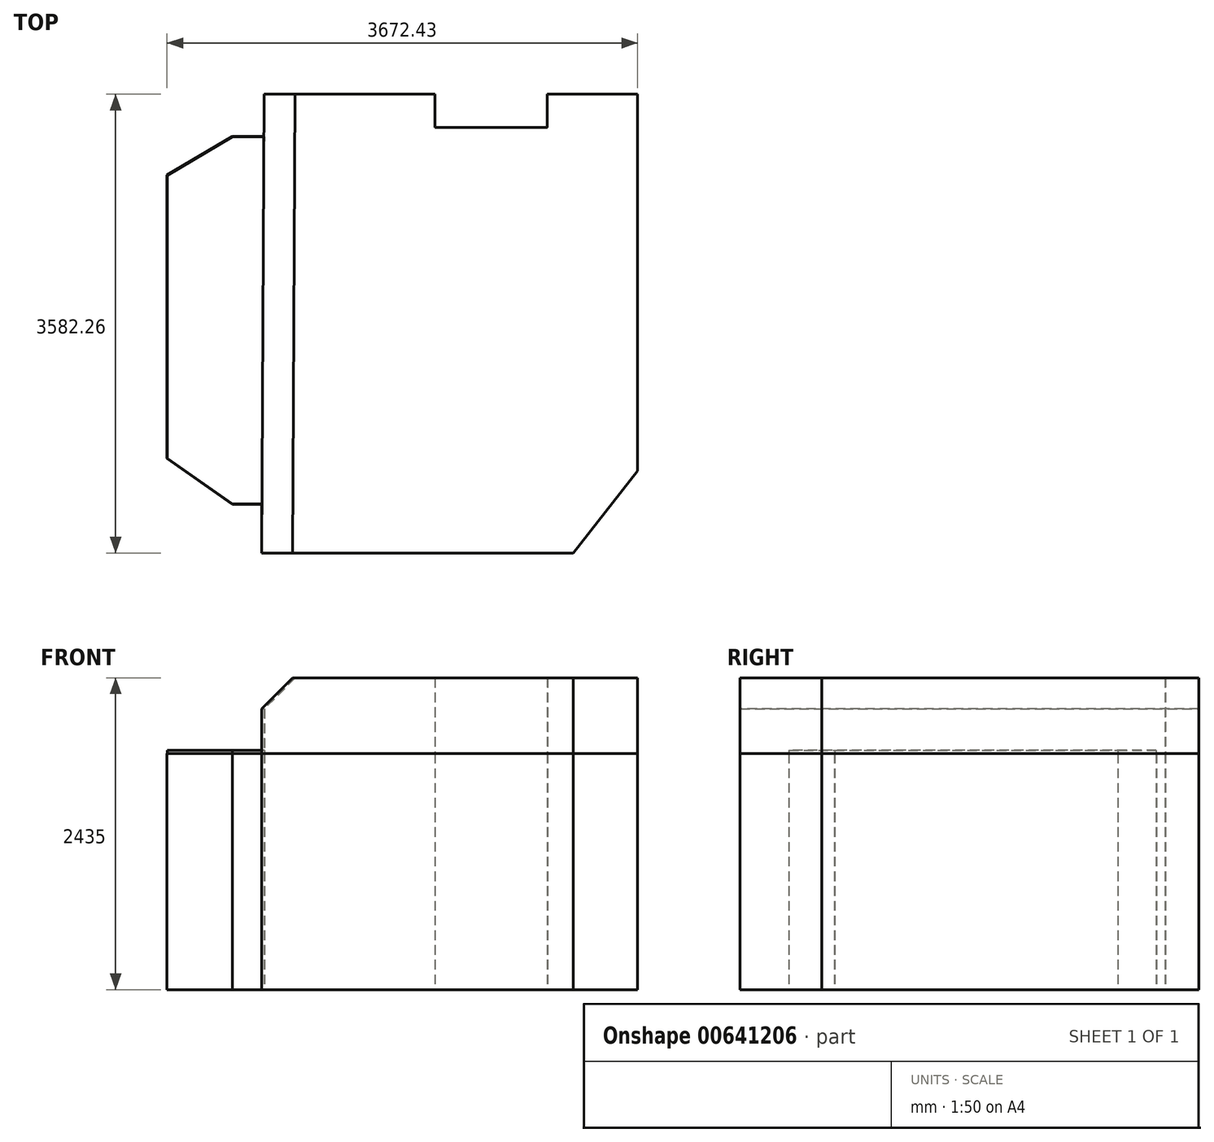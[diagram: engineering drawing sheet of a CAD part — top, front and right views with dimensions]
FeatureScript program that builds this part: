
annotation { "Feature Type Name" : "Feature", "Feature Type Description" : "" }
export const myFeature = defineFeature(function(context is Context, id is Id, definition is map)
    precondition{}
    {
        {
            var Q0;
            Q0=qCreatedBy(makeId("Top.planeOp"),FACE);
            var sketch = newSketch(context, id + "F0", { "sketchPlane" : qUnion([Q0])});
            skLineSegment(sketch, "E0", {"start": v(0, 0) * mm, "end": v(2430, 0) * mm});
            skLineSegment(sketch, "E1", {"start": v(0, 0) * mm, "end": v(0, 380) * mm});
            skLineSegment(sketch, "E2", {"start": v(0, 380) * mm, "end": v(-230, 380) * mm});
            skLineSegment(sketch, "E3", {"start": v(-230, 380) * mm, "end": v(-737.43, 736.24) * mm});
            skLineSegment(sketch, "E4", {"start": v(-737.43, 736.24) * mm, "end": v(-737.43, 2946.24) * mm});
            skLineSegment(sketch, "E5", {"start": v(-737.43, 2946.24) * mm, "end": v(-230, 3247.26) * mm});
            skLineSegment(sketch, "E6", {"start": v(-230, 3247.26) * mm, "end": v(20, 3247.26) * mm});
            skLineSegment(sketch, "E7", {"start": v(20, 3247.26) * mm, "end": v(20, 3577.26) * mm});
            skLineSegment(sketch, "E8", {"start": v(20, 3577.26) * mm, "end": v(1350, 3577.26) * mm});
            skLineSegment(sketch, "E9", {"start": v(1350, 3577.26) * mm, "end": v(1350, 3317.26) * mm});
            skLineSegment(sketch, "E10", {"start": v(1350, 3317.26) * mm, "end": v(2230, 3317.26) * mm});
            skLineSegment(sketch, "E11", {"start": v(2230, 3317.26) * mm, "end": v(2230, 3577.26) * mm});
            skLineSegment(sketch, "E12", {"start": v(2230, 3577.26) * mm, "end": v(2930, 3577.26) * mm});
            skLineSegment(sketch, "E13", {"start": v(2930, 3577.26) * mm, "end": v(2930, 637.26) * mm});
            skLineSegment(sketch, "E14", {"start": v(2930, 637.26) * mm, "end": v(2430, 0) * mm});
            skSolve(sketch);
        }
        {
            var Q0;
            Q0 = qSketchRegion(id + "F0", true);
            extrude(context, id + "F1", {"entities" : qUnion([Q0]), "depth" : 1840 * mm, "offsetDistance" : 25 * mm});
        }
        {
            var Q0;
            Q0=makeQuery(id+"F1.opExtrude","CAP_FACE",FACE,{"disambiguationData":[OSD([sQuery(id+"F0.wireOp",EDGE,"E0"),sQuery(id+"F0.wireOp",EDGE,"E1"),sQuery(id+"F0.wireOp",EDGE,"E2"),sQuery(id+"F0.wireOp",EDGE,"E3"),sQuery(id+"F0.wireOp",EDGE,"E4"),sQuery(id+"F0.wireOp",EDGE,"E5"),sQuery(id+"F0.wireOp",EDGE,"E6"),sQuery(id+"F0.wireOp",EDGE,"E7"),sQuery(id+"F0.wireOp",EDGE,"E8"),sQuery(id+"F0.wireOp",EDGE,"E9"),sQuery(id+"F0.wireOp",EDGE,"E10"),sQuery(id+"F0.wireOp",EDGE,"E11"),sQuery(id+"F0.wireOp",EDGE,"E12"),sQuery(id+"F0.wireOp",EDGE,"E13"),sQuery(id+"F0.wireOp",EDGE,"E14")])],"isStart":false});
            var sketch = newSketch(context, id + "F2", { "sketchPlane" : qUnion([Q0])});
            skLineSegment(sketch, "E15", {"start": v(20, 3247.26) * mm, "end": v(0, 380) * mm});
            skLineSegment(sketch, "E16", {"start": v(0, 380) * mm, "end": v(-230, 380) * mm});
            skLineSegment(sketch, "E17", {"start": v(-230, 380) * mm, "end": v(-737.43, 736.24) * mm});
            skLineSegment(sketch, "E18", {"start": v(-737.43, 736.24) * mm, "end": v(-737.43, 2946.24) * mm});
            skLineSegment(sketch, "E19", {"start": v(-737.43, 2946.24) * mm, "end": v(-230, 3247.26) * mm});
            skLineSegment(sketch, "E20", {"start": v(-230, 3247.26) * mm, "end": v(20, 3247.26) * mm});
            skSolve(sketch);
        }
        {
            var Q0;
            Q0 = qSketchRegion(id + "F2", true);
            extrude(context, id + "F3", {"entities" : qUnion([Q0]), "depth" : 25 * mm, "offsetDistance" : 25 * mm});
        }
        {
            var Q0;
            Q0=makeQuery(id+"F1.opExtrude","CAP_FACE",FACE,{"disambiguationData":[OSD([sQuery(id+"F0.wireOp",EDGE,"E0"),sQuery(id+"F0.wireOp",EDGE,"E1"),sQuery(id+"F0.wireOp",EDGE,"E2"),sQuery(id+"F0.wireOp",EDGE,"E3"),sQuery(id+"F0.wireOp",EDGE,"E4"),sQuery(id+"F0.wireOp",EDGE,"E5"),sQuery(id+"F0.wireOp",EDGE,"E6"),sQuery(id+"F0.wireOp",EDGE,"E7"),sQuery(id+"F0.wireOp",EDGE,"E8"),sQuery(id+"F0.wireOp",EDGE,"E9"),sQuery(id+"F0.wireOp",EDGE,"E10"),sQuery(id+"F0.wireOp",EDGE,"E11"),sQuery(id+"F0.wireOp",EDGE,"E12"),sQuery(id+"F0.wireOp",EDGE,"E13"),sQuery(id+"F0.wireOp",EDGE,"E14")])],"isStart":false});
            var sketch = newSketch(context, id + "F4", { "sketchPlane" : qUnion([Q0])});
            skLineSegment(sketch, "E21", {"start": v(0, 0) * mm, "end": v(20, 3577.26) * mm});
            skLineSegment(sketch, "E22", {"start": v(20, 3577.26) * mm, "end": v(1350, 3577.26) * mm});
            skLineSegment(sketch, "E23", {"start": v(1350, 3577.26) * mm, "end": v(1350, 3317.26) * mm});
            skLineSegment(sketch, "E24", {"start": v(1350, 3317.26) * mm, "end": v(2230, 3317.26) * mm});
            skLineSegment(sketch, "E25", {"start": v(2230, 3317.26) * mm, "end": v(2230, 3577.26) * mm});
            skLineSegment(sketch, "E26", {"start": v(2230, 3577.26) * mm, "end": v(2930, 3577.26) * mm});
            skLineSegment(sketch, "E27", {"start": v(2930, 3577.26) * mm, "end": v(2930, 637.26) * mm});
            skLineSegment(sketch, "E28", {"start": v(2930, 637.26) * mm, "end": v(2430, 0) * mm});
            skLineSegment(sketch, "E29", {"start": v(2430, 0) * mm, "end": v(0, 0) * mm});
            skSolve(sketch);
        }
        {
            var Q0;
            Q0 = qSketchRegion(id + "F4", true);
            extrude(context, id + "F5", {"entities" : qUnion([Q0]), "depth" : 590 * mm, "offsetDistance" : 25 * mm});
        }
        {
            var Q0;
            Q0=makeQuery(id+"F5.opExtrude","CAP_EDGE",EDGE,{"disambiguationData":[OSD([sQuery(id+"F4.wireOp",EDGE,"E21")])],"isStart":false});
            chamfer(context, id + "F6", {"entities" : qUnion([Q0]), "chamferType" : ChamferType.TWO_OFFSETS, "width1" : 240 * mm, "oppositeDirection" : false, "width2" : 240 * mm, "tangentPropagation" : true});
        }
        {
            var Q0;
            Q0=makeQuery(id+"F1.opExtrude","CAP_FACE",FACE,{"disambiguationData":[OSD([sQuery(id+"F0.wireOp",EDGE,"E0"),sQuery(id+"F0.wireOp",EDGE,"E1"),sQuery(id+"F0.wireOp",EDGE,"E2"),sQuery(id+"F0.wireOp",EDGE,"E3"),sQuery(id+"F0.wireOp",EDGE,"E4"),sQuery(id+"F0.wireOp",EDGE,"E5"),sQuery(id+"F0.wireOp",EDGE,"E6"),sQuery(id+"F0.wireOp",EDGE,"E7"),sQuery(id+"F0.wireOp",EDGE,"E8"),sQuery(id+"F0.wireOp",EDGE,"E9"),sQuery(id+"F0.wireOp",EDGE,"E10"),sQuery(id+"F0.wireOp",EDGE,"E11"),sQuery(id+"F0.wireOp",EDGE,"E12"),sQuery(id+"F0.wireOp",EDGE,"E13"),sQuery(id+"F0.wireOp",EDGE,"E14")])],"isStart":false});
            shell(context, id + "F7", {"entities" : qUnion([Q0]), "thickness" : 2.5 * mm, "oppositeDirection" : true});
        }
        {
            var Q0;
            Q0=makeQuery(id+"F5.opExtrude","CAP_FACE",FACE,{"disambiguationData":[OSD([sQuery(id+"F4.wireOp",EDGE,"E21"),sQuery(id+"F4.wireOp",EDGE,"E22"),sQuery(id+"F4.wireOp",EDGE,"E23"),sQuery(id+"F4.wireOp",EDGE,"E24"),sQuery(id+"F4.wireOp",EDGE,"E25"),sQuery(id+"F4.wireOp",EDGE,"E26"),sQuery(id+"F4.wireOp",EDGE,"E27"),sQuery(id+"F4.wireOp",EDGE,"E28"),sQuery(id+"F4.wireOp",EDGE,"E29")])],"isStart":true});
            shell(context, id + "F8", {"entities" : qUnion([Q0]), "thickness" : 2.5 * mm, "oppositeDirection" : true});
        }
    });
